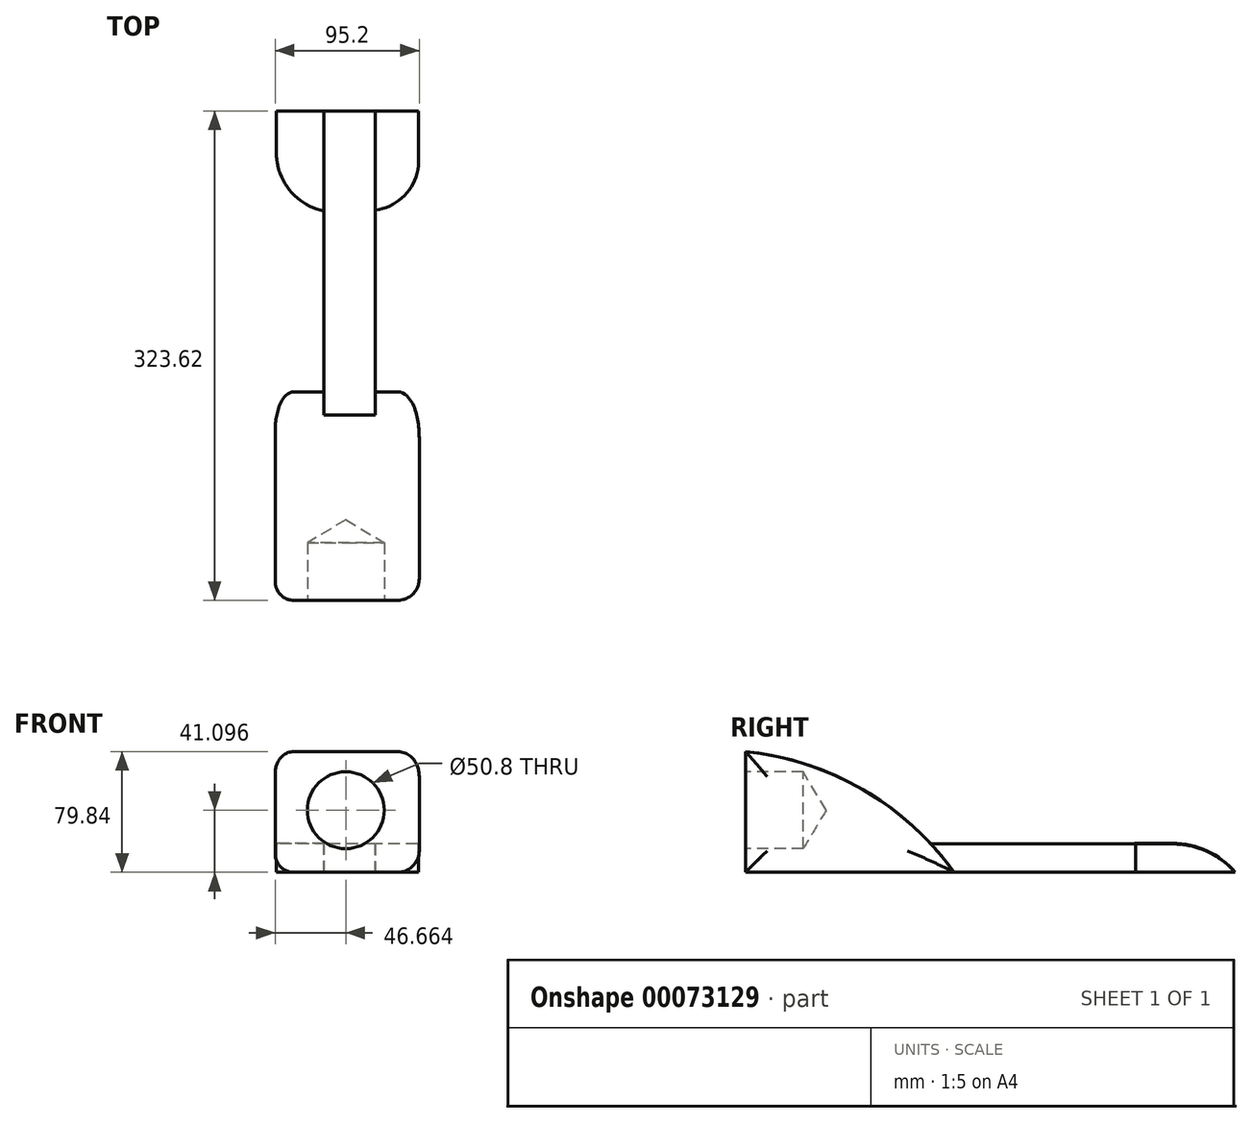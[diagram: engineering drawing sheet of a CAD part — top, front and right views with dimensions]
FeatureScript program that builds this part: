
annotation { "Feature Type Name" : "Feature", "Feature Type Description" : "" }
export const myFeature = defineFeature(function(context is Context, id is Id, definition is map)
    precondition{}
    {
        {
            var Q0;
            Q0=qCreatedBy(makeId("Right.planeOp"),FACE);
            var sketch = newSketch(context, id + "F0", { "sketchPlane" : qUnion([Q0])});
            skLineSegment(sketch, "E0.bottom", {"start": v(-75.3, 18.72) * mm, "end": v(185.8, 18.72) * mm});
            skLineSegment(sketch, "E0.top", {"start": v(-75.3, 0) * mm, "end": v(185.8, 0) * mm});
            skLineSegment(sketch, "E0.left", {"start": v(-75.3, 18.72) * mm, "end": v(-75.3, 0) * mm});
            skLineSegment(sketch, "E0.right", {"start": v(185.8, 18.72) * mm, "end": v(185.8, 0) * mm});
            skSolve(sketch);
        }
        {
            var Q0;
            Q0=makeQuery(id+"F0.imprint","IMPRINT",FACE,{"disambiguationData":[TD([[makeQuery(id+"F0.imprint","IMPRINT",EDGE,{"derivedFrom":sQuery(id+"F0.wireOp",EDGE,"E0.bottom")}),-1.0]])]});
            extrude(context, id + "F1", {"entities" : qUnion([Q0]), "depth" : 33.95 * mm});
        }
        {
            var Q0;
            Q0=makeQuery(id+"F1.opExtrude","SWEPT_FACE",FACE,{"disambiguationData":[OSD([sQuery(id+"F0.wireOp",EDGE,"E0.top")])]});
            var sketch = newSketch(context, id + "F2", { "sketchPlane" : qUnion([Q0])});
            skLineSegment(sketch, "E1", {"start": v(0, -185.8) * mm, "end": v(-31.42, -185.8) * mm});
            skLineSegment(sketch, "E2", {"start": v(-31.42, -185.8) * mm, "end": v(-31.42, -158.37) * mm});
            skArc(sketch, "E3", {"start": v(-31.42, -158.37) * mm, "mid": v(-22.58, -133.4) * mm, "end": v(0, -119.53) * mm});
            skLineSegment(sketch, "E4", {"start": v(0, -119.53) * mm, "end": v(0, -185.8) * mm});
            skSolve(sketch);
        }
        {
            var Q0;
            Q0=makeQuery(id+"F2.imprint","IMPRINT",FACE,{"disambiguationData":[TD([[makeQuery(id+"F2.imprint","IMPRINT",EDGE,{"derivedFrom":sQuery(id+"F2.wireOp",EDGE,"E1")}),-1.0]])]});
            extrude(context, id + "F3", {"entities" : qUnion([Q0]), "oppositeDirection" : true, "depth" : 19.3 * mm});
        }
        {
            var Q0;
            Q0=makeQuery(id+"F1.opExtrude","SWEPT_FACE",FACE,{"disambiguationData":[OSD([sQuery(id+"F0.wireOp",EDGE,"E0.top")])]});
            var sketch = newSketch(context, id + "F4", { "sketchPlane" : qUnion([Q0])});
            skLineSegment(sketch, "E5", {"start": v(33.95, -185.8) * mm, "end": v(62.69, -185.8) * mm});
            skLineSegment(sketch, "E6", {"start": v(62.69, -185.8) * mm, "end": v(62.69, -152.87) * mm});
            skArc(sketch, "E7", {"start": v(62.69, -152.87) * mm, "mid": v(54.48, -131.1) * mm, "end": v(33.95, -120.18) * mm});
            skSolve(sketch);
        }
        {
            var Q0;
            {var subQ0=sQuery(id+"F4.wireOp",EDGE,"E5");Q0=makeQuery(id+"F4.imprint","IMPRINT",FACE,{"disambiguationData":[TD([[makeQuery(id+"F4.imprint","IMPRINT",EDGE,{"derivedFrom":subQ0}),1.0]])]});}
            extrude(context, id + "F5", {"entities" : qUnion([Q0]), "oppositeDirection" : true, "depth" : 18.76 * mm});
        }
        {
            var Q0;
            Q0=qCreatedBy(makeId("Front.planeOp"),FACE);
            var sketch = newSketch(context, id + "F6", { "sketchPlane" : qUnion([Q0])});
            skLineSegment(sketch, "E8.bottom", {"start": v(-32.17, 80.82) * mm, "end": v(63.03, 80.82) * mm});
            skLineSegment(sketch, "E8.top", {"start": v(-32.17, 0) * mm, "end": v(63.03, 0) * mm});
            skLineSegment(sketch, "E8.left", {"start": v(-32.17, 80.82) * mm, "end": v(-32.17, 0) * mm});
            skLineSegment(sketch, "E8.right", {"start": v(63.03, 80.82) * mm, "end": v(63.03, 0) * mm});
            skSolve(sketch);
        }
        {
            var Q0;
            Q0=makeQuery(id+"F6.imprint","IMPRINT",FACE,{"disambiguationData":[TD([[makeQuery(id+"F6.imprint","IMPRINT",EDGE,{"derivedFrom":sQuery(id+"F6.wireOp",EDGE,"E8.bottom")}),-1.0]])]});
            extrude(context, id + "F7", {"entities" : qUnion([Q0]), "operationType" : NewBodyOperationType.ADD, "depth" : 137.83 * mm});
        }
        {
            var Q0;
            Q0=makeQuery(id+"F7.opExtrude","CAP_EDGE",EDGE,{"disambiguationData":[OSD([sQuery(id+"F6.wireOp",EDGE,"E8.bottom")])],"isStart":true});
            fillet(context, id + "F8", {"entities" : qUnion([Q0]), "radius" : 193.42 * mm, "tangentPropagation" : true, "allowEdgeOverflow" : false});
        }
        {
            var Q0;
            Q0=makeQuery(id+"F7.opExtrude","SWEPT_FACE",FACE,{"disambiguationData":[OSD([sQuery(id+"F6.wireOp",EDGE,"E8.right")])]});
            fillet(context, id + "F9", {"entities" : qUnion([Q0]), "radius" : 14.23 * mm, "tangentPropagation" : true, "allowEdgeOverflow" : false});
        }
        {
            var Q0;
            Q0=makeQuery(id+"F7.opExtrude","SWEPT_FACE",FACE,{"disambiguationData":[OSD([sQuery(id+"F6.wireOp",EDGE,"E8.left")])]});
            fillet(context, id + "F10", {"entities" : qUnion([Q0]), "radius" : 12.35 * mm, "tangentPropagation" : true, "allowEdgeOverflow" : false});
        }
        {
            var Q0;
            Q0=makeQuery(id+"F7.opExtrude","CAP_FACE",FACE,{"disambiguationData":[OSD([sQuery(id+"F6.wireOp",EDGE,"E8.bottom"),sQuery(id+"F6.wireOp",EDGE,"E8.top"),sQuery(id+"F6.wireOp",EDGE,"E8.left"),sQuery(id+"F6.wireOp",EDGE,"E8.right")])],"isStart":false});
            var sketch = newSketch(context, id + "F11", { "sketchPlane" : qUnion([Q0])});
            skCircle(sketch, "E9", {"center": v(14.5, 41.1) * mm, "radius": 23.77 * mm});
            skPoint(sketch, "E9.centerSnap0", {"position": v(14.5, 0) * mm});
            skSolve(sketch);
        }
        {
            var Q0;
            Q0=sQuery(id+"F11.wireOp",VERTEX,"E9.center");
            var Q1;
            Q1=makeQuery(id+"F1.opExtrude","SWEPT_BODY",BODY,{"disambiguationData":[OSD([sQuery(id+"F0.wireOp",EDGE,"E0.bottom"),sQuery(id+"F0.wireOp",EDGE,"E0.top"),sQuery(id+"F0.wireOp",EDGE,"E0.left"),sQuery(id+"F0.wireOp",EDGE,"E0.right")])]});
            hole(context, id + "F12", {"style" : HoleStyle.SIMPLE, "holeDiameter" : 50.8 * mm, "endStyle" : HoleEndStyle.BLIND, "holeDepth" : 38.1 * mm, "locations" : qUnion([Q0]), "scope" : qUnion([Q1])});
        }
        {
            var Q0;
            Q0=makeQuery(id+"F1.opExtrude","SWEPT_EDGE",EDGE,{"disambiguationData":[OSD([sQuery(id+"F0.wireOp",EDGE,"E0.bottom"),sQuery(id+"F0.wireOp",EDGE,"E0.right")])]});
            var Q1;
            Q1=makeQuery(id+"F3.opExtrude","CAP_EDGE",EDGE,{"disambiguationData":[OSD([sQuery(id+"F2.wireOp",EDGE,"E1")])],"isStart":false});
            fillet(context, id + "F13", {"entities" : qUnion([Q0, Q1]), "radius" : 54.1 * mm, "tangentPropagation" : true, "allowEdgeOverflow" : false});
        }
        {
            var Q0;
            Q0=makeQuery(id+"F5.opExtrude","CAP_EDGE",EDGE,{"disambiguationData":[OSD([sQuery(id+"F4.wireOp",EDGE,"E5")])],"isStart":false});
            fillet(context, id + "F14", {"entities" : qUnion([Q0]), "radius" : 54.48 * mm, "tangentPropagation" : true, "allowEdgeOverflow" : false});
        }
    });
